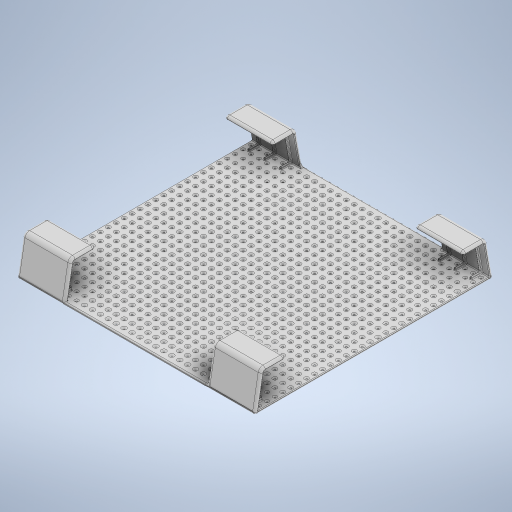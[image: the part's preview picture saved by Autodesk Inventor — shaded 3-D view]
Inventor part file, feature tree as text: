
AUTODESK INVENTOR PART (.ipt)
format: ipt  version: 2023 (Build 270158030, 158C)  size: 4,183,040 bytes
history: native  units: mm
features: fillet x15, extrude x5, sketch x4, plane x3, mirror x2, pattern_linear x1
ambient origin geometry x8: Origin, YZ Plane, XZ Plane, XY Plane, X Axis, Y Axis, Z Axis, Center Point
bodies: Solid1 (feature_tree)
feature tree (30):
  extrude  "Extrusion1"  Depth=150.0mm
  extrude  "Extrusion2"  Depth=1.5mm
  extrude  "Extrusion4"  Depth=120.0mm
  plane  "Work Plane1"
  extrude  "Extrusion5"  Depth=0.7mm TaperAngle=0.0deg
  fillet  "Fillet8"  Radius=1.0mm
  pattern_linear  "Rectangular Pattern1"  Spacing1=2.5mm  [1 undecoded]
  fillet  "Fillet13"  Radius=5.0mm
  fillet  "Fillet14"  Radius=300.0mm
  fillet  "Fillet15"  Radius=2.5mm
  plane  "Work Plane2"
  mirror  "Mirror1"
  plane  "Work Plane4"
  mirror  "Mirror3"
  fillet  "Fillet16"  Radius=5.0mm
  fillet  "Fillet17"  Radius=20.0mm
  fillet  "Fillet18"  Radius=2.0mm
  fillet  "Fillet19"  Radius=2.0mm
  extrude  "Extrusion3"  Depth=0.7mm
  fillet  "Fillet20"  Radius=15.0mm
  fillet  "Fillet21"  Radius=2.0mm
  fillet  "Fillet22"  Radius=2.0mm
  fillet  "Fillet23"  Radius=13.962634mm
  fillet  "Fillet24"  Radius=15.0mm
  fillet  "Fillet25"  Radius=30.0mm
  fillet  "Fillet26"  Radius=30.0mm
  sketch  "Sketch1"  dims[d0=150.0mm d1=150.0mm]
  sketch  "Sketch3"  dims[d2=1.5mm d3=0.0mm d4=3.0mm]
  sketch  "Sketch4"  dims[d5=90.0deg d6=120.0mm]
  sketch  "Sketch7"  dims[d7=90.0deg d8=3.0mm d9=0.0mm d10=1.0mm d11=2.5mm d12=5.0mm d13=300.0mm d15=5.0mm d16=300.0mm d18=5.0mm d21=2.5mm d23=5.0mm d24=0.0mm d29=20.0mm d30=2.0mm d31=2.0mm d32=13.962634mm d33=15.0mm d34=2.0mm d35=2.0mm d36=13.962634mm d37=15.0mm d41=30.0mm d42=30.0mm d43=10.0mm d44=10.0mm d45=1.5mm d46=0.0mm d48=6.0mm d49=1.3mm d50=1.3mm d51=1.3mm d52=7.0mm d53=-5.0mm d54=1.0mm d55=0.0mm d56=0.45mm d61=30.0mm d63=10.0mm d64=0.4mm d65=0.4mm d66=0.39mm d67=3.0mm d68=1.5mm d69=0.4mm d70=1.0mm d71=1.0mm d72=1.0mm d73=1.0mm d74=1.0mm d75=1.0mm d76=1.0mm d77=0.7mm d27=0.0mm d28=0.0mm]
note: 1 required parameter value undecoded (feature->parameter linkage not recoverable at this tier; creation-order binding heuristic only, values carry confidence <= 0.55)
